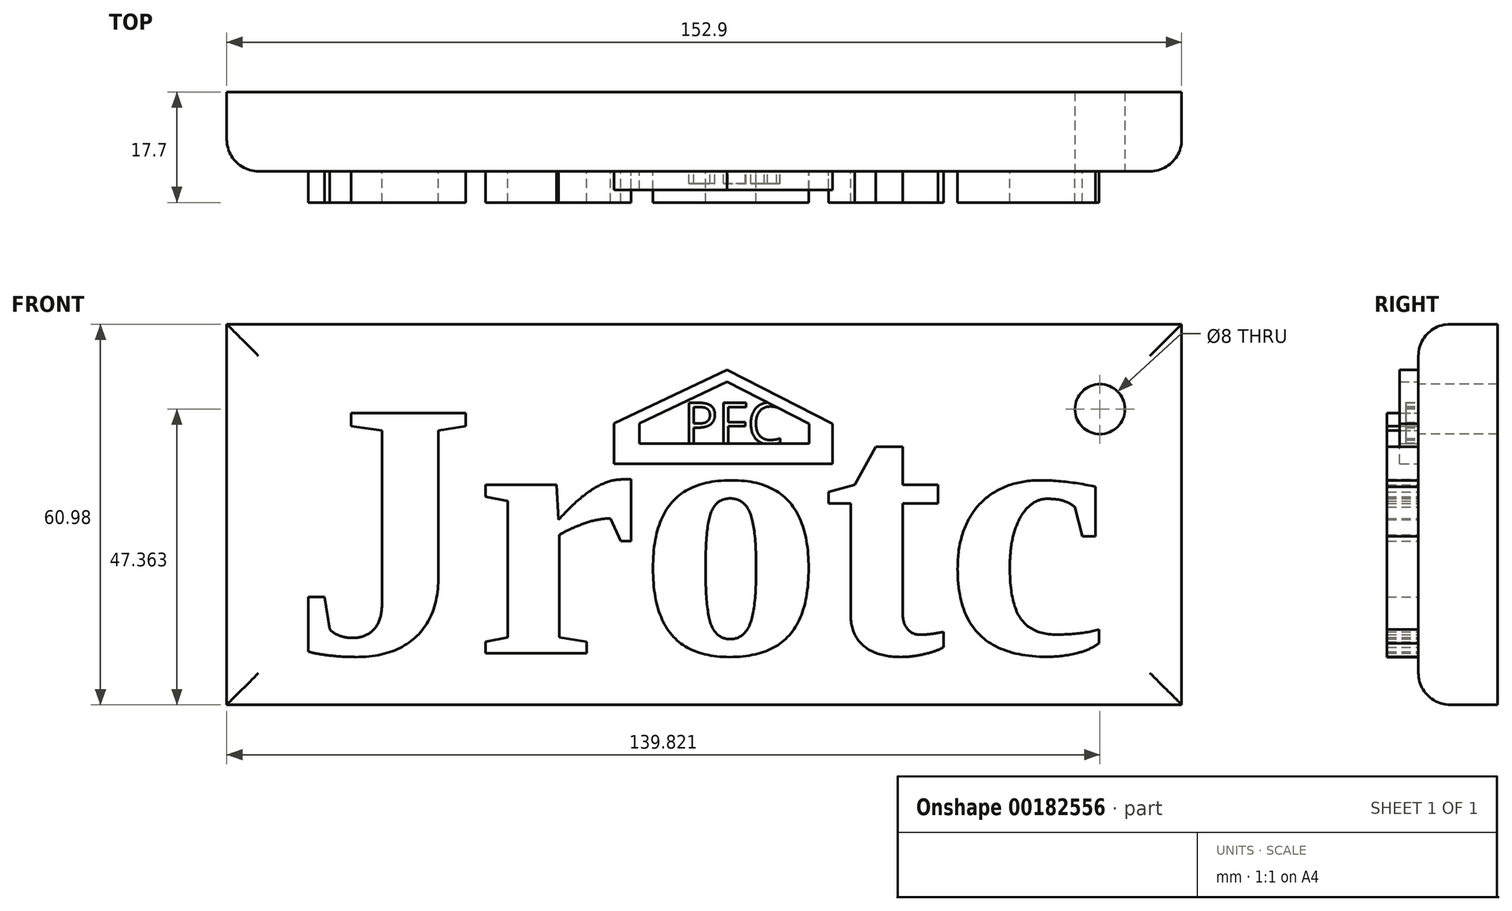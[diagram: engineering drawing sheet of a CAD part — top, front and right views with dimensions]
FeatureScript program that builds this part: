
annotation { "Feature Type Name" : "Feature", "Feature Type Description" : "" }
export const myFeature = defineFeature(function(context is Context, id is Id, definition is map)
    precondition{}
    {
        {
            var Q0;
            Q0=qCreatedBy(makeId("Front.planeOp"),FACE);
            var sketch = newSketch(context, id + "F0", { "sketchPlane" : qUnion([Q0])});
            skLineSegment(sketch, "E0.bottom", {"start": v(-76.45, 30.49) * mm, "end": v(76.45, 30.49) * mm});
            skLineSegment(sketch, "E0.top", {"start": v(-76.45, -30.49) * mm, "end": v(76.45, -30.49) * mm});
            skLineSegment(sketch, "E0.left", {"start": v(-76.45, 30.49) * mm, "end": v(-76.45, -30.49) * mm});
            skLineSegment(sketch, "E0.right", {"start": v(76.45, 30.49) * mm, "end": v(76.45, -30.49) * mm});
            skPoint(sketch, "E0.middle", {"position": v(0, 0) * mm});
            skSolve(sketch);
        }
        {
            var Q0;
            Q0 = qSketchRegion(id + "F0", true);
            extrude(context, id + "F1", {"entities" : qUnion([Q0]), "depth" : 12.7 * mm});
        }
        {
            var Q0;
            Q0=makeQuery(id+"F1.opExtrude","CAP_FACE",FACE,{"disambiguationData":[OSD([sQuery(id+"F0.wireOp",EDGE,"E0.bottom"),sQuery(id+"F0.wireOp",EDGE,"E0.top"),sQuery(id+"F0.wireOp",EDGE,"E0.left"),sQuery(id+"F0.wireOp",EDGE,"E0.right")])],"isStart":false});
            fillet(context, id + "F2", {"entities" : qUnion([Q0]), "radius" : 5.08 * mm, "tangentPropagation" : true, "allowEdgeOverflow" : false});
        }
        {
            var Q0;
            Q0=makeQuery(id+"F1.opExtrude","CAP_FACE",FACE,{"disambiguationData":[OSD([sQuery(id+"F0.wireOp",EDGE,"E0.bottom"),sQuery(id+"F0.wireOp",EDGE,"E0.top"),sQuery(id+"F0.wireOp",EDGE,"E0.left"),sQuery(id+"F0.wireOp",EDGE,"E0.right")])],"isStart":false});
            var sketch = newSketch(context, id + "F3", { "sketchPlane" : qUnion([Q0])});
            skText(sketch, "E1", { "text": "Jrotc", "fontName": "Tinos-Bold.ttf"});
            const initialGuessF3  = {"E1": [-0.066, -0.02226, 1, 0, 0.04237]};
            skSetInitialGuess(sketch, initialGuessF3);
            skSolve(sketch);
        }
        {
            var Q0;
            Q0 = qSketchRegion(id + "F3", true);
            extrude(context, id + "F4", {"entities" : qUnion([Q0]), "operationType" : NewBodyOperationType.ADD, "depth" : 5 * mm});
        }
        {
            var Q0;
            {var subQ0=sQuery(id+"F0.wireOp",EDGE,"E0.bottom");var subQ1=sQuery(id+"F0.wireOp",EDGE,"E0.top");var subQ2=sQuery(id+"F0.wireOp",EDGE,"E0.left");var subQ3=sQuery(id+"F0.wireOp",EDGE,"E0.right");Q0=makeQuery(id+"F4.boolean.opBoolean","SPLIT",FACE,{"disambiguationData":[TD([makeQuery(id+"F2.opFillet","BLEND_FACE",FACE,{"disambiguationData":[OSD([subQ0])]})])],"derivedFrom":makeQuery(id+"F1.opExtrude","CAP_FACE",FACE,{"disambiguationData":[OSD([subQ0,subQ1,subQ2,subQ3])],"isStart":false})});}
            var sketch = newSketch(context, id + "F5", { "sketchPlane" : qUnion([Q0])});
            skLineSegment(sketch, "E2", {"start": v(-14.43, 8.14) * mm, "end": v(20.57, 8.14) * mm});
            skLineSegment(sketch, "E3", {"start": v(20.57, 8.14) * mm, "end": v(20.57, 14.55) * mm});
            skLineSegment(sketch, "E4", {"start": v(-14.43, 8.14) * mm, "end": v(-14.43, 14.62) * mm});
            skLineSegment(sketch, "E5", {"start": v(-14.43, 14.62) * mm, "end": v(3.68, 23.18) * mm});
            skLineSegment(sketch, "E6", {"start": v(3.68, 23.18) * mm, "end": v(20.57, 14.55) * mm});
            skLineSegment(sketch, "E7", {"start": v(5.64, 22.18) * mm, "end": v(-14.43, 12.7) * mm});
            skLineSegment(sketch, "E8", {"start": v(-10.37, 14.62) * mm, "end": v(-10.37, 8.14) * mm});
            skLineSegment(sketch, "E9", {"start": v(3.68, 21.26) * mm, "end": v(20.57, 12.63) * mm});
            skLineSegment(sketch, "E10", {"start": v(16.81, 14.55) * mm, "end": v(16.81, 8.14) * mm});
            skLineSegment(sketch, "E11", {"start": v(16.81, 11.34) * mm, "end": v(-10.37, 11.34) * mm});
            skSolve(sketch);
        }
        {
            var Q0;
            Q0 = qSketchRegion(id + "F5", true);
            extrude(context, id + "F6", {"entities" : qUnion([Q0]), "operationType" : NewBodyOperationType.ADD, "depth" : 3 * mm});
        }
        {
            var Q0;
            {var subQ0=sQuery(id+"F0.wireOp",EDGE,"E0.bottom");var subQ1=sQuery(id+"F0.wireOp",EDGE,"E0.top");var subQ2=sQuery(id+"F0.wireOp",EDGE,"E0.left");var subQ3=sQuery(id+"F0.wireOp",EDGE,"E0.right");Q0=makeQuery(id+"F6.boolean.opBoolean","SPLIT",FACE,{"disambiguationData":[TD([makeQuery(id+"F6.opExtrude","SWEPT_FACE",FACE,{"disambiguationData":[OSD([sQuery(id+"F5.wireOp",EDGE,"E7")])]})])],"derivedFrom":makeQuery(id+"F4.boolean.opBoolean","SPLIT",FACE,{"disambiguationData":[TD([makeQuery(id+"F2.opFillet","BLEND_FACE",FACE,{"disambiguationData":[OSD([subQ0])]})])],"derivedFrom":makeQuery(id+"F1.opExtrude","CAP_FACE",FACE,{"disambiguationData":[OSD([subQ0,subQ1,subQ2,subQ3])],"isStart":false})})});}
            var sketch = newSketch(context, id + "F7", { "sketchPlane" : qUnion([Q0])});
            skText(sketch, "E12", { "text": "PFC", "fontName": "OpenSans-Regular.ttf"});
            const initialGuessF7  = {"E12": [-0.00334, 0.01134, 1, 0, 0.0066]};
            skSetInitialGuess(sketch, initialGuessF7);
            skSolve(sketch);
        }
        {
            var Q0;
            Q0 = qSketchRegion(id + "F7", true);
            extrude(context, id + "F8", {"entities" : qUnion([Q0]), "operationType" : NewBodyOperationType.ADD, "depth" : 2 * mm});
        }
        {
            var Q0;
            {var subQ31=sQuery(id+"F0.wireOp",EDGE,"E0.bottom");var subQ32=makeQuery(id+"F2.opFillet","BLEND_FACE",FACE,{"disambiguationData":[OSD([subQ31])]});var subQ37=sQuery(id+"F0.wireOp",EDGE,"E0.top");var subQ41=sQuery(id+"F0.wireOp",EDGE,"E0.left");var subQ43=sQuery(id+"F0.wireOp",EDGE,"E0.right");Q0=makeQuery(id+"F6.boolean.opBoolean","SPLIT",FACE,{"disambiguationData":[TD([subQ32])],"derivedFrom":makeQuery(id+"F4.boolean.opBoolean","SPLIT",FACE,{"disambiguationData":[TD([subQ32])],"derivedFrom":makeQuery(id+"F1.opExtrude","CAP_FACE",FACE,{"disambiguationData":[OSD([subQ31,subQ37,subQ41,subQ43])],"isStart":false})})});}
            var sketch = newSketch(context, id + "F9", { "sketchPlane" : qUnion([Q0])});
            skCircle(sketch, "E13", {"center": v(63.37, 16.87) * mm, "radius": 4 * mm});
            skSolve(sketch);
        }
        {
            var Q0;
            Q0 = qSketchRegion(id + "F9", true);
            extrude(context, id + "F10", {"entities" : qUnion([Q0]), "operationType" : NewBodyOperationType.REMOVE, "endBound" : BoundingType.THROUGH_ALL, "oppositeDirection" : true, "depth" : 25 * mm});
        }
    });
